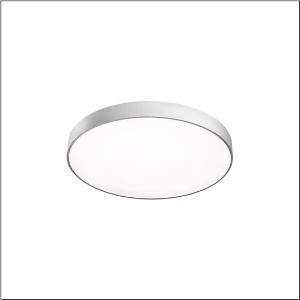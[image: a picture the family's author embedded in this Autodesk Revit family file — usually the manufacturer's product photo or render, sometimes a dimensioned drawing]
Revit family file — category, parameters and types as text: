
# Revit family: round_21_m_51mr36fd0321s
name_source: partatom
category: Lighting Fixtures
units: mm (PartAtom-declared; Revit-internal decimal feet)

## family parameters
Cut with Voids When Loaded = No
Host = Face
Light Source = No
Part Type = Normal
Room Calculation Point = No
Round Connector Dimension = Use Diameter
Shared = No

## types (1)
- Round 21 M (1 x LED, 7500 lm, 54.9 W, 3000K)
    Apparent Load = 55 VA
    CIE Flux Codes = 49 80 96 100 100
    Color Rendering = 80
    Color Temperature = 3000K
    Default Elevation = 1800 mm
    Description = Round 21 M, wall and ceiling luminaire, primary optical cover: cover, of PMMA, opal, light emission: direct distribution, primary light characteristic: symmetric, installation type: suspended mounting, surface-mounted, LED, rated luminous flux: 7.500lm, luminous efficacy: 137lm/W, light colour: 830, colour temperature: 3000K, control gear: DALI 2, with terminal, 5-pole, mains connection: 230V, AC, 50/60Hz, rated input power: 54.8W, housing, of aluminium, coated, silver, diameter: 600mm, height: 62mm, protection rating (complete): IP40, insulation class (complete): insulation class I (protective earthing), certification: CE, impact resistance: IK04, permissible operating ambient temperature: -10..+35°C, packaging unit: 1 piece
    Height = 87 mm
    Lamp = 1 x LED
    Lamp Light Flux = 7500 lm
    Lamp Power = 54.9 W
    Lamp count = 1
    Length = 600 mm
    Luminous efficacy = 137 lm/W
    Manufacturer = Siteco
    ModVariant = No
    Model = 51MR36FD0321S
    Mounting Place = Ceiling
    Mounting Type = Surface mounted
    Number of Poles = 1
    OnlyDefault = Yes
    Power Factor = 1
    Product Name = Round 21 M
    Product group = wall and ceiling luminaire | ceiling mounted
    ProductGroupID = 304
    Protection Class = Protection class I
    Protection Degree = IP 40
    RLX_Detail_Level = 1
    RLX_Emergency_Light_Flux = 0 lm
    RLX_Emergency_Type = 0
    RLX_Emergency_Type_DB = No
    RlxData = <blob elided: 14845 chars, md5=0708c2eb>
    Socket = socket
    Standby Power = 0 W
    System Light Flux = 7500 lm
    System Power = 55 W
    Type Comments = Product without accessories
    Type Image = l_1258303.jpg
    URL = http://relux.com
    VarID = ---
    Voltage = 0 V
    Weight = 0.00 kg
    Width = 0 mm  [stored 0 ft]

note: [stored X ft] marks values corroborated as IEEE doubles in the binary element streams (Revit-internal decimal feet)

## geometry (parser evidence)
native form markers: Sweep x13
no freeform markers — native parametric forms only
